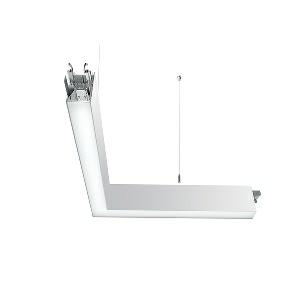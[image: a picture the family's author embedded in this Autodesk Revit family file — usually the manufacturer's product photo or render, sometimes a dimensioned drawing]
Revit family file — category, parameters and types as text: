
# Revit family: idoo_line_-_ilp_3000_840_d_lr_mid_00807701_3d65
name_source: partatom
category: Lighting Fixtures
units: mm (PartAtom-declared; Revit-internal decimal feet)

## family parameters
Cut with Voids When Loaded = No
Host = Face
Light Source = No
Part Type = Normal
Room Calculation Point = No
Round Connector Dimension = Use Diameter
Shared = No

## types (1)
- IDOO.line - ILP 3000/840/D/LR MID (1 x LED, 3150 lm, 4000K)
    Apparent Load = 23 VA
    Approval mark = CE
    CIE Flux Codes = 66 91 98 40 100
    Color Rendering = 80-89
    Color Temperature = 4000K
    Control Gear = Electronic ballast
    Default Elevation = 1800 mm
    Description = ILP 3000/840/D|Suspended luminaire|light source: LED|connected load: 220-240 V, 50/60 Hz|Power consumption: approx. 23 W|standby: approx. 0,20|luminous flux: 3150 lm|luminous efficacy: 136 lm/W|light distribution: Direct/indirect|direct ratio: approx. 40 %|colour temperature: Cold white, ca. 4000 K|color rendering index (CRI): >= 80|chromaticity tolerance:  3 SDCM|System of protection: IP 40|technology: Continuously dimmable|luminaire body|material: Sectional aluminium|colour: White|lamp cover: Acrylic (PMMA), Clear|Fastening: Steel cable 0.3 - 0.7 m|glare control: Prism aperture|luminance(L65): <= 2700 cd/m|unified glare rating(4H 8H): <=  16|special features: DALI Load 1x, TouchDIM - dimming via standard switch, Through-wired, up to 18 m on one mains connection, Flicker-free, Continous light without dark z, Suitable as emergency lighting, 90░ rerouting on the right sid, Mechanical and electrical connection of the individual modules without tools|
    Frequency = 50 Hz
    Height = 110 mm
    Lamp = 1 x LED
    Lamp Light Flux = 3150 lm
    Lamp count = 1
    Length = 600 mm
    Luminous efficacy = 137 lm/W
    Manufacturer = Waldmann
    ModVariant = No
    Model = 00807701
    Mounting Place = Ceiling
    Mounting Type = Pendant
    Number of Poles = 1
    OnlyDefault = Yes
    Power Factor = 1
    Product Name = IDOO.line - ILP 3000/840/D/LR MID
    Product group = Suspended luminaire
    ProductGroupID = 9
    Protection Class = Protection class I
    Protection Degree = IP 40
    RLX_Detail_Level = 1
    RLX_Emergency_Light_Flux = 0 lm
    RLX_Emergency_Type = 0
    RLX_Emergency_Type_DB = No
    RlxData = <blob elided: 20997 chars, md5=1dbbabe9>
    Socket = socket
    Standby Power = 0 W
    System Light Flux = 3150 lm
    System Power = 23 W
    Type Comments = Product without accessories
    Type Image = ilp_dlp_lr_ws.jpg
    URL = http://relux.com
    VarID = ---
    Voltage = 230 V
    Voltage Range = 220-240 V
    Weight = 0.00 kg
    Width = 600 mm

## geometry (parser evidence)
native form markers: Blend x4, Sweep x14
no freeform markers — native parametric forms only
